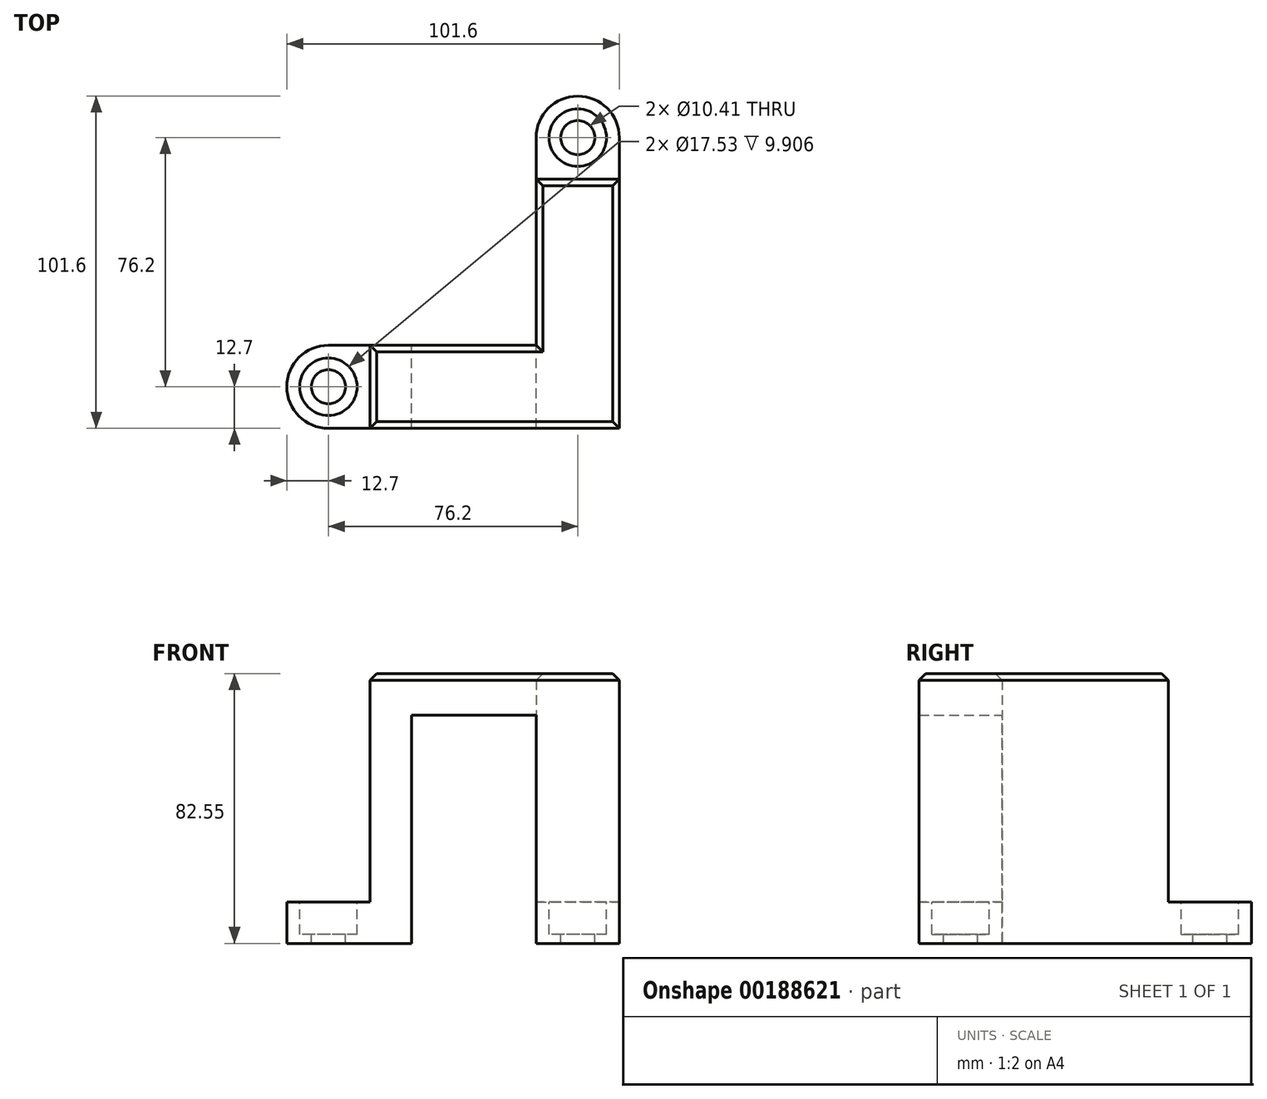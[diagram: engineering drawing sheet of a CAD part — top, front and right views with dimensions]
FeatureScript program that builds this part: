
annotation { "Feature Type Name" : "Feature", "Feature Type Description" : "" }
export const myFeature = defineFeature(function(context is Context, id is Id, definition is map)
    precondition{}
    {
        {
            var Q0;
            Q0=qCreatedBy(makeId("Top.planeOp"),FACE);
            var sketch = newSketch(context, id + "F0", { "sketchPlane" : qUnion([Q0])});
            skLineSegment(sketch, "E0", {"start": v(0, 0) * mm, "end": v(-72.5, 0) * mm});
            skLineSegment(sketch, "E1", {"start": v(-25.4, 25.4) * mm, "end": v(-25.4, 88.9) * mm});
            skLineSegment(sketch, "E2", {"start": v(-76.2, 0) * mm, "end": v(-76.2, 25.4) * mm});
            skLineSegment(sketch, "E3", {"start": v(-25.4, 76.2) * mm, "end": v(0, 76.2) * mm});
            skPoint(sketch, "E4", {"position": v(-88.9, 12.7) * mm});
            skPoint(sketch, "E5", {"position": v(-12.7, 88.9) * mm});
            skArc(sketch, "E6", {"start": v(-101.6, 12.7) * mm, "mid": v(-97.88, 21.68) * mm, "end": v(-88.9, 25.4) * mm});
            skArc(sketch, "E7", {"start": v(-88.9, 0) * mm, "mid": v(-97.88, 3.72) * mm, "end": v(-101.6, 12.7) * mm});
            skLineSegment(sketch, "E8", {"start": v(-72.5, 0) * mm, "end": v(-88.9, 0) * mm});
            skArc(sketch, "E9", {"start": v(-12.7, 101.6) * mm, "mid": v(-3.72, 97.88) * mm, "end": v(0, 88.9) * mm});
            skArc(sketch, "E10", {"start": v(-12.7, 101.6) * mm, "mid": v(-21.68, 97.88) * mm, "end": v(-25.4, 88.9) * mm});
            skLineSegment(sketch, "E11", {"start": v(0, 88.9) * mm, "end": v(0, 0) * mm});
            skLineSegment(sketch, "E12", {"start": v(-25.4, 88.9) * mm, "end": v(-25.4, 88.9) * mm});
            skPoint(sketch, "E13", {"position": v(-63.5, 12.7) * mm});
            skPoint(sketch, "E14", {"position": v(-63.5, 25.4) * mm});
            skLineSegment(sketch, "E15", {"start": v(-25.4, 25.4) * mm, "end": v(-63.5, 25.4) * mm});
            skLineSegment(sketch, "E16", {"start": v(-76.2, 25.4) * mm, "end": v(-88.9, 25.4) * mm});
            skLineSegment(sketch, "E17", {"start": v(-63.5, 25.4) * mm, "end": v(-76.2, 25.4) * mm});
            skSolve(sketch);
        }
        {
            var Q0;
            {var subQ5=sQuery(id+"F0.wireOp",EDGE,"E0");Q0=makeQuery(id+"F0.imprint","IMPRINT",FACE,{"disambiguationData":[TD([[makeQuery(id+"F0.imprint","IMPRINT",EDGE,{"derivedFrom":subQ5}),-1.0]])]});}
            extrude(context, id + "F1", {"entities" : qUnion([Q0]), "depth" : 82.55 * mm});
        }
        {
            var Q0;
            Q0 = qSketchRegion(id + "F0", true);
            extrude(context, id + "F2", {"entities" : qUnion([Q0]), "operationType" : NewBodyOperationType.ADD, "depth" : 12.7 * mm});
        }
        {
            var Q0;
            {var subQ0=sQuery(id+"F0.wireOp",EDGE,"E1");var subQ1=sQuery(id+"F0.wireOp",EDGE,"E11");var subQ2=sQuery(id+"F0.wireOp",EDGE,"E10");var subQ3=sQuery(id+"F0.wireOp",EDGE,"E9");Q0=makeQuery(id+"F2.boolean.opBoolean","SPLIT",FACE,{"disambiguationData":[TD([makeQuery(id+"F1.opExtrude","SWEPT_FACE",FACE,{"disambiguationData":[OSD([subQ0])]})])],"derivedFrom":makeQuery(id+"F2.opExtrude","CAP_FACE",FACE,{"disambiguationData":[OSD([sQuery(id+"F0.wireOp",EDGE,"E0"),subQ0,sQuery(id+"F0.wireOp",EDGE,"E6"),sQuery(id+"F0.wireOp",EDGE,"E7"),sQuery(id+"F0.wireOp",EDGE,"b6cbcea7-8d39-41f6-a6e2-f5b133982fde"),sQuery(id+"F0.wireOp",EDGE,"E8"),subQ3,subQ2,subQ1])],"isStart":false})});}
            var sketch = newSketch(context, id + "F3", { "sketchPlane" : qUnion([Q0])});
            skPoint(sketch, "E18", {"position": v(-12.7, 88.9) * mm});
            skSolve(sketch);
        }
        {
            var Q0;
            Q0=sQuery(id+"F3.wireOp",VERTEX,"E18");
            var Q1;
            Q1=makeQuery(id+"F1.opExtrude","SWEPT_BODY",BODY,{"disambiguationData":[OSD([sQuery(id+"F0.wireOp",EDGE,"E0"),sQuery(id+"F0.wireOp",EDGE,"E1"),sQuery(id+"F0.wireOp",EDGE,"E2"),sQuery(id+"F0.wireOp",EDGE,"E3"),sQuery(id+"F0.wireOp",EDGE,"b6cbcea7-8d39-41f6-a6e2-f5b133982fde"),sQuery(id+"F0.wireOp",EDGE,"E8"),sQuery(id+"F0.wireOp",EDGE,"E11")])]});
            hole(context, id + "F4", {"style" : HoleStyle.C_BORE, "endStyle" : HoleEndStyle.THROUGH, "holeDiameter" : 10.4 * mm, "cBoreDiameter" : 17.53 * mm, "cBoreDepth" : 9.9 * mm, "locations" : qUnion([Q0]), "scope" : qUnion([Q1]), "isTappedThrough" : true});
        }
        {
            var Q0;
            {var subQ0=sQuery(id+"F0.wireOp",EDGE,"E8");var subQ1=sQuery(id+"F0.wireOp",EDGE,"E0");var subQ2=sQuery(id+"F0.wireOp",EDGE,"b6cbcea7-8d39-41f6-a6e2-f5b133982fde");var subQ3=sQuery(id+"F0.wireOp",EDGE,"E7");var subQ4=sQuery(id+"F0.wireOp",EDGE,"E6");Q0=makeQuery(id+"F2.boolean.opBoolean","SPLIT",FACE,{"disambiguationData":[TD([makeQuery(id+"F1.opExtrude","SWEPT_FACE",FACE,{"disambiguationData":[OSD([sQuery(id+"F0.wireOp",EDGE,"E2")])]})])],"derivedFrom":makeQuery(id+"F2.opExtrude","CAP_FACE",FACE,{"disambiguationData":[OSD([subQ1,sQuery(id+"F0.wireOp",EDGE,"E1"),subQ4,subQ3,subQ2,subQ0,sQuery(id+"F0.wireOp",EDGE,"E9"),sQuery(id+"F0.wireOp",EDGE,"E10"),sQuery(id+"F0.wireOp",EDGE,"E11")])],"isStart":false})});}
            var sketch = newSketch(context, id + "F5", { "sketchPlane" : qUnion([Q0])});
            skPoint(sketch, "E19", {"position": v(-88.9, 12.7) * mm});
            skSolve(sketch);
        }
        {
            var Q0;
            Q0=sQuery(id+"F5.wireOp",VERTEX,"E19");
            var Q1;
            Q1=makeQuery(id+"F1.opExtrude","SWEPT_BODY",BODY,{"disambiguationData":[OSD([sQuery(id+"F0.wireOp",EDGE,"E0"),sQuery(id+"F0.wireOp",EDGE,"E1"),sQuery(id+"F0.wireOp",EDGE,"E2"),sQuery(id+"F0.wireOp",EDGE,"E3"),sQuery(id+"F0.wireOp",EDGE,"b6cbcea7-8d39-41f6-a6e2-f5b133982fde"),sQuery(id+"F0.wireOp",EDGE,"E8"),sQuery(id+"F0.wireOp",EDGE,"E11")])]});
            hole(context, id + "F6", {"style" : HoleStyle.C_BORE, "endStyle" : HoleEndStyle.THROUGH, "holeDiameter" : 10.4 * mm, "cBoreDiameter" : 17.53 * mm, "cBoreDepth" : 9.9 * mm, "locations" : qUnion([Q0]), "scope" : qUnion([Q1]), "isTappedThrough" : true});
        }
        {
            var Q0;
            {var subQ0=sQuery(id+"F0.wireOp",EDGE,"E17");var subQ1=sQuery(id+"F0.wireOp",EDGE,"E15");Q0=makeQuery(id+"F2.boolean.opBoolean","MERGE",FACE,{"derivedFrom":[makeQuery(id+"F1.opExtrude","SWEPT_FACE",FACE,{"disambiguationData":[OSD([subQ1,subQ0])]}),makeQuery(id+"F2.opExtrude","SWEPT_FACE",FACE,{"disambiguationData":[OSD([subQ1,sQuery(id+"F0.wireOp",EDGE,"E16"),subQ0])]})]});}
            var sketch = newSketch(context, id + "F7", { "sketchPlane" : qUnion([Q0])});
            skLineSegment(sketch, "E20", {"start": v(63.5, 0) * mm, "end": v(63.5, 69.85) * mm});
            skLineSegment(sketch, "E21", {"start": v(63.5, 69.85) * mm, "end": v(25.4, 69.85) * mm});
            skSolve(sketch);
        }
        {
            var Q0;
            {var subQ0=sQuery(id+"F7.wireOp",EDGE,"E20");Q0=makeQuery(id+"F7.imprint","IMPRINT",FACE,{"disambiguationData":[TD([[makeQuery(id+"F7.imprint","IMPRINT",EDGE,{"derivedFrom":subQ0}),1.0]])]});}
            extrude(context, id + "F8", {"entities" : qUnion([Q0]), "operationType" : NewBodyOperationType.REMOVE, "oppositeDirection" : true, "depth" : 25.4 * mm});
        }
        {
            var Q0;
            Q0=makeQuery(id+"F1.opExtrude","CAP_EDGE",EDGE,{"disambiguationData":[OSD([sQuery(id+"F0.wireOp",EDGE,"E11")])],"isStart":false});
            chamfer(context, id + "F9", {"entities" : qUnion([Q0]), "width" : 2.03 * mm, "tangentPropagation" : true});
        }
        {
            var Q0;
            Q0=makeQuery(id+"F1.opExtrude","CAP_EDGE",EDGE,{"disambiguationData":[OSD([sQuery(id+"F0.wireOp",EDGE,"E0"),sQuery(id+"F0.wireOp",EDGE,"E8")])],"isStart":false});
            chamfer(context, id + "F10", {"entities" : qUnion([Q0]), "width" : 2.03 * mm, "tangentPropagation" : true});
        }
        {
            var Q0;
            Q0=makeQuery(id+"F1.opExtrude","CAP_EDGE",EDGE,{"disambiguationData":[OSD([sQuery(id+"F0.wireOp",EDGE,"E1")])],"isStart":false});
            chamfer(context, id + "F11", {"entities" : qUnion([Q0]), "width" : 2.03 * mm, "tangentPropagation" : true});
        }
        {
            var Q0;
            Q0=makeQuery(id+"F1.opExtrude","CAP_EDGE",EDGE,{"disambiguationData":[OSD([sQuery(id+"F0.wireOp",EDGE,"E15"),sQuery(id+"F0.wireOp",EDGE,"E17")])],"isStart":false});
            chamfer(context, id + "F12", {"entities" : qUnion([Q0]), "width" : 2.03 * mm, "tangentPropagation" : true});
        }
        {
            var Q0;
            Q0=makeQuery(id+"F1.opExtrude","CAP_EDGE",EDGE,{"disambiguationData":[OSD([sQuery(id+"F0.wireOp",EDGE,"E3")])],"isStart":false});
            chamfer(context, id + "F13", {"entities" : qUnion([Q0]), "width" : 2.03 * mm, "tangentPropagation" : true});
        }
        {
            var Q0;
            Q0=makeQuery(id+"F1.opExtrude","CAP_EDGE",EDGE,{"disambiguationData":[OSD([sQuery(id+"F0.wireOp",EDGE,"E2")])],"isStart":false});
            chamfer(context, id + "F14", {"entities" : qUnion([Q0]), "width" : 2.03 * mm, "tangentPropagation" : true});
        }
    });
